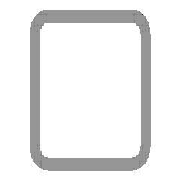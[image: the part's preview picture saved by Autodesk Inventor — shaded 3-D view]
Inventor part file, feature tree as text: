
AUTODESK INVENTOR PART (.ipt)
format: ipt  version: 2025 (Build 290162010, 162A)  size: 142,336 bytes
history: native  units: mm (DEFAULTED — no unit token found)
features: other x4, plane x2, split x1, sketch x1
ambient origin geometry x8: Origin, YZ Plane, XZ Plane, XY Plane, X Axis, Y Axis, Z Axis, Center Point
bodies: Solid1 (feature_tree), Body (feature_tree)
feature tree (8):
  parser-record x1  (decoder bookkeeping rows leaked as tree rows — omitted from the tree; the rows remain in map.json)
  other  "Driven Length"
  other  "Start Plane"
  other  "End Plane"
  plane  "Work Plane4"
  split  "Split1"
  sketch  "Sketch3"  dims[d3=440.0mm d4=0.0mm d7=4.0mm d9=40.0mm d11=40.0mm d12=2.0mm d13=-0.0mm d14=440.0mm d15=20.0mm d16=20.0mm d17=90.0deg d18=440.0mm]
  plane  "Work Plane3"
